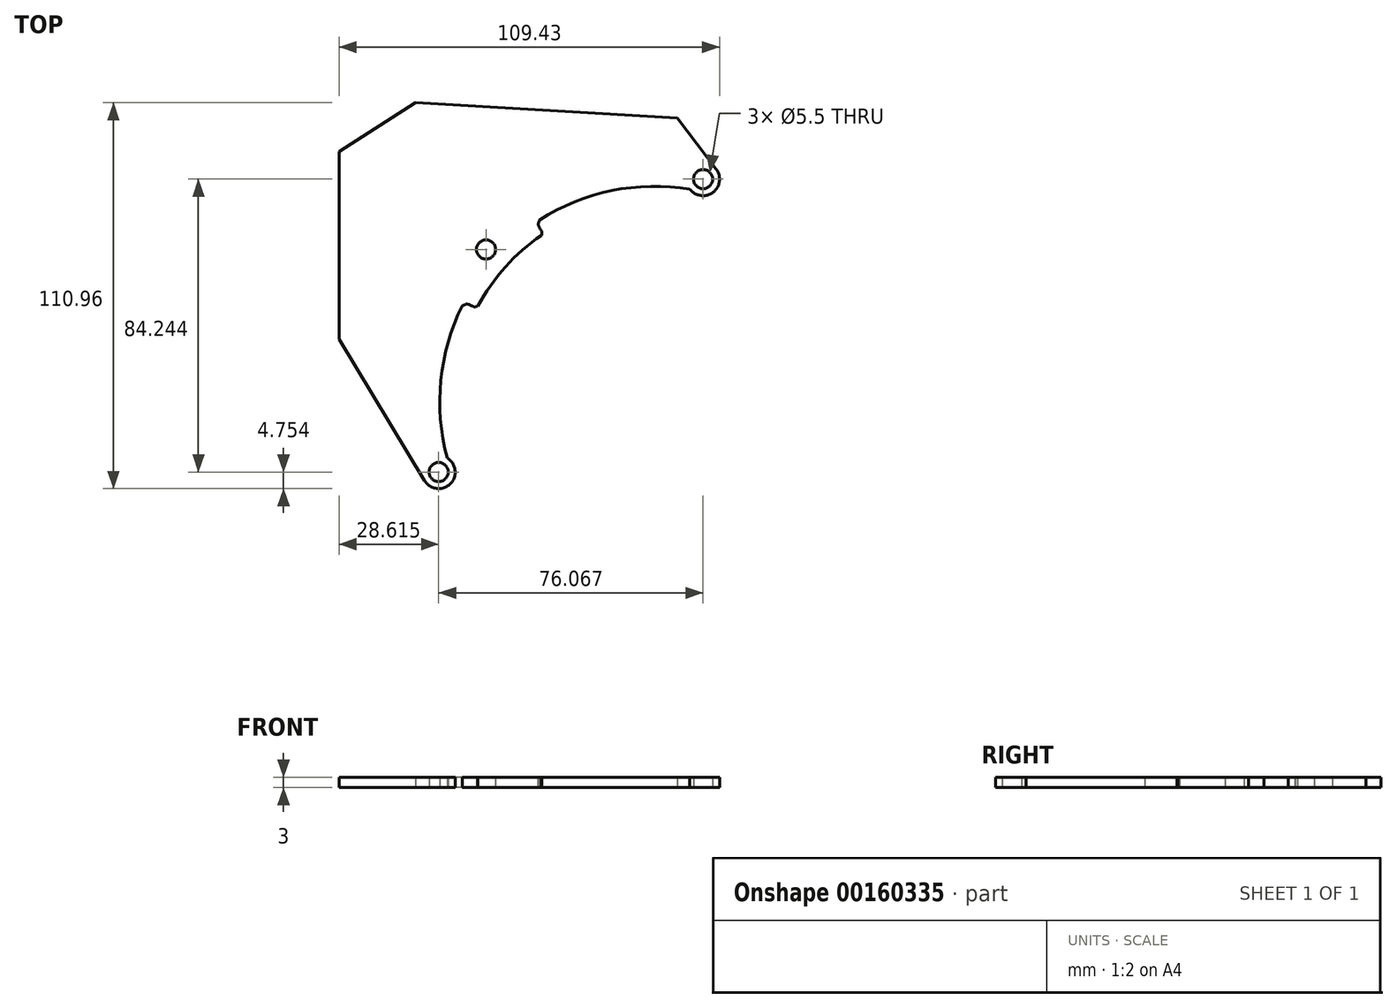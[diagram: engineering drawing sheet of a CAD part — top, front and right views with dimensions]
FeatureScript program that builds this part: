
annotation { "Feature Type Name" : "Feature", "Feature Type Description" : "" }
export const myFeature = defineFeature(function(context is Context, id is Id, definition is map)
    precondition{}
    {
        {
            var Q0;
            Q0=qCreatedBy(makeId("Top.planeOp"),FACE);
            var sketch = newSketch(context, id + "F0", { "sketchPlane" : qUnion([Q0])});
            skLineSegment(sketch, "E0", {"start": v(20.9, -3.89) * mm, "end": v(20.9, -13.89) * mm});
            skCircle(sketch, "E1", {"center": v(13.76, 64.04) * mm, "radius": 2.75 * mm});
            skCircle(sketch, "E2", {"center": v(0, 0) * mm, "radius": 65.5 * mm, "construction": true});
            skCircle(sketch, "E3", {"center": v(-48.68, 43.82) * mm, "radius": 2.75 * mm});
            skCircle(sketch, "E4", {"center": v(-62.3, -20.2) * mm, "radius": 2.75 * mm});
            skLineSegment(sketch, "E5", {"start": v(0, 0) * mm, "end": v(0, 50) * mm, "construction": true});
            skLineSegment(sketch, "E6", {"start": v(0, 0) * mm, "end": v(-50, 0) * mm, "construction": true});
            skLineSegment(sketch, "E7", {"start": v(13.76, 64.04) * mm, "end": v(0, 0) * mm, "construction": true});
            skLineSegment(sketch, "E8", {"start": v(-48.68, 43.82) * mm, "end": v(0, 0) * mm, "construction": true});
            skLineSegment(sketch, "E9", {"start": v(-62.3, -20.2) * mm, "end": v(0, 0) * mm, "construction": true});
            skArc(sketch, "E10", {"start": v(-55.17, -17.9) * mm, "mid": v(57.76, -5.24) * mm, "end": v(-51.05, 27.53) * mm});
            skArc(sketch, "E11", {"start": v(-57.94, -22.07) * mm, "mid": v(46.02, -41.55) * mm, "end": v(16.06, 59.88) * mm});
            skArc(sketch, "E12", {"start": v(-66.37, -22.66) * mm, "mid": v(-58.94, -23.56) * mm, "end": v(-59.86, -16.13) * mm});
            skArc(sketch, "E13", {"start": v(9.96, 61.2) * mm, "mid": v(16.62, 60.24) * mm, "end": v(17.55, 66.9) * mm});
            skLineSegment(sketch, "E14", {"start": v(-66.37, -22.66) * mm, "end": v(-90.92, 18) * mm});
            skLineSegment(sketch, "E15", {"start": v(-90.92, 18) * mm, "end": v(-90.92, 72) * mm});
            skLineSegment(sketch, "E16", {"start": v(-90.92, 72) * mm, "end": v(-69, 86) * mm});
            skLineSegment(sketch, "E17", {"start": v(-69, 86) * mm, "end": v(6.37, 81.65) * mm});
            skLineSegment(sketch, "E18", {"start": v(6.37, 81.65) * mm, "end": v(17.55, 66.9) * mm});
            skFitSpline(sketch, "E19", {"points": [v(-55.5, 27.62) * mm, v(-54.32, 28.09) * mm, v(-53.26, 27.86) * mm, v(-52.1, 27.3) * mm, v(-51.05, 27.53) * mm], "startDerivative": vector(4.4, 2.43) * mm, "endDerivative": vector(4.62, 1.73) * mm});
            skFitSpline(sketch, "E20.MirrorCS", {"points": [v(-33.29, 52.3) * mm, v(-33.62, 51.08) * mm, v(-33.29, 50.05) * mm, v(-32.61, 48.96) * mm, v(-32.72, 47.89) * mm], "startDerivative": vector(-1.95, -4.64) * mm, "endDerivative": vector(-1.23, -4.77) * mm});
            skArc(sketch, "E21.trimOffspring", {"start": v(9.96, 61.2) * mm, "mid": v(-12.48, 60.73) * mm, "end": v(-33.29, 52.3) * mm});
            skArc(sketch, "E22.trimOffspring", {"start": v(-55.5, 27.62) * mm, "mid": v(-61.7, 6.15) * mm, "end": v(-59.86, -16.13) * mm});
            skSolve(sketch);
        }
        {
            var Q0;
            Q0=makeQuery(id+"F0.imprint","IMPRINT",FACE,{"disambiguationData":[TD([[makeQuery(id+"F0.imprint","IMPRINT",EDGE,{"derivedFrom":sQuery(id+"F0.wireOp",EDGE,"E1")}),-1.0]])]});
            extrude(context, id + "F1", {"entities" : qUnion([Q0]), "depth" : 3 * mm, "offsetDistance" : 25 * mm});
        }
    });
